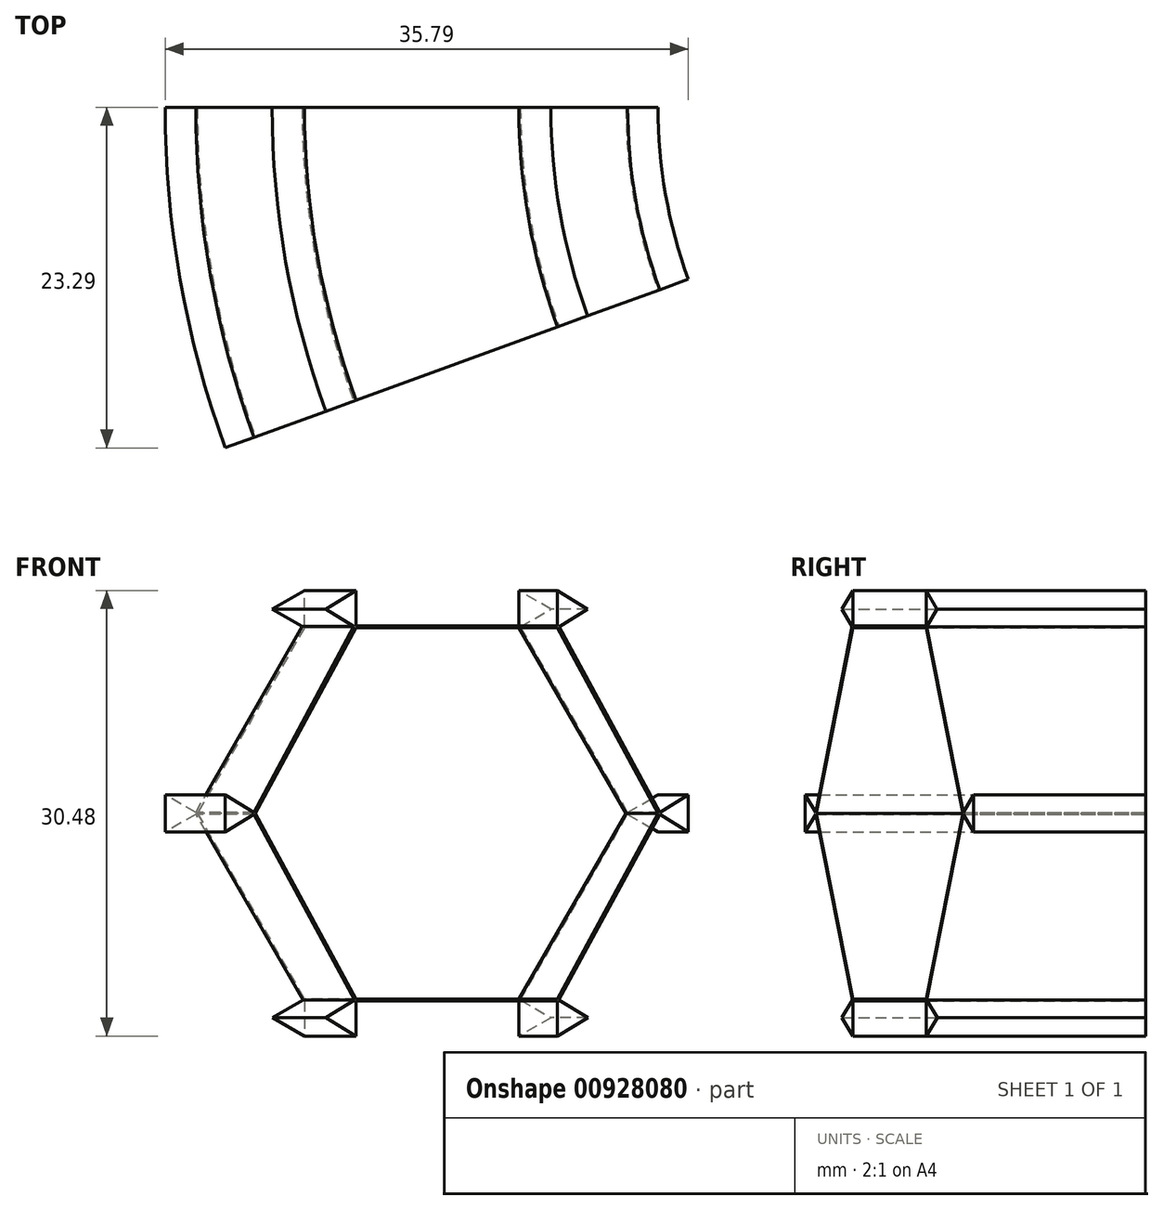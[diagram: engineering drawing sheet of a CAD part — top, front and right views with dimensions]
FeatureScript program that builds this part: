
annotation { "Feature Type Name" : "Feature", "Feature Type Description" : "" }
export const myFeature = defineFeature(function(context is Context, id is Id, definition is map)
    precondition{}
    {
        {
            var Q0;
            Q0=qCreatedBy(makeId("Top.planeOp"),FACE);
            var sketch = newSketch(context, id + "F0", { "sketchPlane" : qUnion([Q0])});
            skLineSegment(sketch, "E0", {"start": v(0, 0) * mm, "end": v(-50.8, 0) * mm});
            skCircle(sketch, "E1", {"center": v(0, 0) * mm, "radius": 50.8 * mm});
            skSolve(sketch);
        }
        {
            var Q0;
            Q0=qCreatedBy(makeId("Front.planeOp"),FACE);
            var sketch = newSketch(context, id + "F1", { "sketchPlane" : qUnion([Q0])});
            skPoint(sketch, "E2.0.midPoint", {"position": v(-51.22, 12.7) * mm});
            skLineSegment(sketch, "E3", {"start": v(-65.88, 0) * mm, "end": v(-68.08, -1.27) * mm});
            skLineSegment(sketch, "E4", {"start": v(-58.55, -12.7) * mm, "end": v(-60.75, -13.97) * mm});
            skLineSegment(sketch, "E5", {"start": v(-58.55, -12.7) * mm, "end": v(-58.55, -15.23) * mm});
            skLineSegment(sketch, "E6", {"start": v(-43.88, -12.7) * mm, "end": v(-43.88, -15.23) * mm});
            skLineSegment(sketch, "E7", {"start": v(-43.88, -12.7) * mm, "end": v(-41.67, -13.98) * mm});
            skLineSegment(sketch, "E8", {"start": v(-36.55, 0) * mm, "end": v(-34.36, -1.26) * mm});
            skLineSegment(sketch, "E9", {"start": v(-36.55, 0) * mm, "end": v(-34.36, 1.26) * mm});
            skLineSegment(sketch, "E10", {"start": v(-43.88, 12.7) * mm, "end": v(-41.7, 13.97) * mm});
            skLineSegment(sketch, "E11", {"start": v(-58.55, 12.7) * mm, "end": v(-58.55, 15.25) * mm});
            skLineSegment(sketch, "E12", {"start": v(-43.88, 12.7) * mm, "end": v(-43.88, 15.25) * mm});
            skLineSegment(sketch, "E13", {"start": v(-58.55, 12.7) * mm, "end": v(-60.76, 13.98) * mm});
            skLineSegment(sketch, "E14", {"start": v(-65.88, 0) * mm, "end": v(-68.08, 1.27) * mm});
            skLineSegment(sketch, "E15", {"start": v(-51.22, 12.7) * mm, "end": v(-51.22, 0) * mm});
            skLineSegment(sketch, "E16", {"start": v(-34.36, 1.26) * mm, "end": v(-34.36, -1.26) * mm});
            skLineSegment(sketch, "E17", {"start": v(-41.67, -13.98) * mm, "end": v(-43.88, -15.23) * mm});
            skLineSegment(sketch, "E18", {"start": v(-58.55, -15.23) * mm, "end": v(-60.75, -13.97) * mm});
            skLineSegment(sketch, "E19", {"start": v(-68.08, -1.27) * mm, "end": v(-68.08, 1.27) * mm});
            skLineSegment(sketch, "E20", {"start": v(-58.55, 15.25) * mm, "end": v(-60.76, 13.98) * mm});
            skLineSegment(sketch, "E21", {"start": v(-41.7, 13.97) * mm, "end": v(-43.88, 15.25) * mm});
            skLineSegment(sketch, "E22", {"start": v(-36.55, 0) * mm, "end": v(-36.33, -0.13) * mm});
            skLineSegment(sketch, "E23", {"start": v(-43.78, -12.76) * mm, "end": v(-43.88, -12.7) * mm});
            skLineSegment(sketch, "E24", {"start": v(-43.78, -12.76) * mm, "end": v(-36.44, -0.06) * mm});
            skLineSegment(sketch, "E25", {"start": v(-36.44, -0.06) * mm, "end": v(-36.55, 0) * mm});
            skLineSegment(sketch, "E26", {"start": v(-36.55, 0) * mm, "end": v(-43.88, -12.7) * mm});
            skLineSegment(sketch, "E27", {"start": v(-43.88, -12.7) * mm, "end": v(-43.88, -12.82) * mm});
            skLineSegment(sketch, "E28", {"start": v(-43.88, -12.82) * mm, "end": v(-58.55, -12.82) * mm});
            skLineSegment(sketch, "E29", {"start": v(-58.55, -12.82) * mm, "end": v(-58.55, -12.7) * mm});
            skLineSegment(sketch, "E30", {"start": v(-58.55, -12.7) * mm, "end": v(-43.88, -12.7) * mm});
            skLineSegment(sketch, "E31", {"start": v(-58.55, -12.7) * mm, "end": v(-58.66, -12.76) * mm});
            skLineSegment(sketch, "E32", {"start": v(-58.66, -12.76) * mm, "end": v(-65.95, -0.13) * mm});
            skLineSegment(sketch, "E33", {"start": v(-65.95, -0.13) * mm, "end": v(-66, -0.06) * mm});
            skLineSegment(sketch, "E34", {"start": v(-66, -0.06) * mm, "end": v(-65.88, 0) * mm});
            skLineSegment(sketch, "E35", {"start": v(-65.88, 0) * mm, "end": v(-58.55, -12.7) * mm});
            skLineSegment(sketch, "E36", {"start": v(-65.88, 0) * mm, "end": v(-66, 0.06) * mm});
            skLineSegment(sketch, "E37", {"start": v(-66, 0.06) * mm, "end": v(-58.71, 12.8) * mm});
            skLineSegment(sketch, "E38", {"start": v(-58.71, 12.8) * mm, "end": v(-58.55, 12.7) * mm});
            skLineSegment(sketch, "E39", {"start": v(-58.55, 12.7) * mm, "end": v(-65.88, 0) * mm});
            skLineSegment(sketch, "E40", {"start": v(-58.55, 12.7) * mm, "end": v(-58.55, 12.84) * mm});
            skLineSegment(sketch, "E41", {"start": v(-58.55, 12.84) * mm, "end": v(-43.88, 12.84) * mm});
            skLineSegment(sketch, "E42", {"start": v(-43.88, 12.84) * mm, "end": v(-43.88, 12.7) * mm});
            skLineSegment(sketch, "E43", {"start": v(-43.88, 12.7) * mm, "end": v(-58.55, 12.7) * mm});
            skLineSegment(sketch, "E44", {"start": v(-36.55, 0) * mm, "end": v(-36.44, 0.07) * mm});
            skLineSegment(sketch, "E45", {"start": v(-36.44, 0.07) * mm, "end": v(-43.78, 12.78) * mm});
            skLineSegment(sketch, "E46", {"start": v(-43.78, 12.78) * mm, "end": v(-43.88, 12.7) * mm});
            skLineSegment(sketch, "E47", {"start": v(-43.88, 12.7) * mm, "end": v(-36.55, 0) * mm});
            skSolve(sketch);
        }
        {
            var Q0;
            {var subQ3=sQuery(id+"F1.wireOp",EDGE,"E46");Q0=makeQuery(id+"F1.imprint","IMPRINT",FACE,{"disambiguationData":[TD([[makeQuery(id+"F1.imprint","IMPRINT",EDGE,{"derivedFrom":subQ3}),1.0]])]});}
            var Q1;
            {var subQ2=sQuery(id+"F1.wireOp",EDGE,"E16");Q1=makeQuery(id+"F1.imprint","IMPRINT",FACE,{"disambiguationData":[TD([[makeQuery(id+"F1.imprint","IMPRINT",EDGE,{"derivedFrom":subQ2}),-1.0]])]});}
            var Q2;
            {var subQ2=sQuery(id+"F1.wireOp",EDGE,"E20");Q2=makeQuery(id+"F1.imprint","IMPRINT",FACE,{"disambiguationData":[TD([[makeQuery(id+"F1.imprint","IMPRINT",EDGE,{"derivedFrom":subQ2}),1.0]])]});}
            var Q3;
            {var subQ4=sQuery(id+"F1.wireOp",EDGE,"E17");Q3=makeQuery(id+"F1.imprint","IMPRINT",FACE,{"disambiguationData":[TD([[makeQuery(id+"F1.imprint","IMPRINT",EDGE,{"derivedFrom":subQ4}),-1.0]])]});}
            var Q4;
            {var subQ4=sQuery(id+"F1.wireOp",EDGE,"E18");Q4=makeQuery(id+"F1.imprint","IMPRINT",FACE,{"disambiguationData":[TD([[makeQuery(id+"F1.imprint","IMPRINT",EDGE,{"derivedFrom":subQ4}),-1.0]])]});}
            var Q5;
            {var subQ4=sQuery(id+"F1.wireOp",EDGE,"E19");Q5=makeQuery(id+"F1.imprint","IMPRINT",FACE,{"disambiguationData":[TD([[makeQuery(id+"F1.imprint","IMPRINT",EDGE,{"derivedFrom":subQ4}),-1.0]])]});}
            var Q6;
            {var subQ3=sQuery(id+"F1.wireOp",EDGE,"E47");Q6=makeQuery(id+"F1.imprint","IMPRINT",FACE,{"disambiguationData":[TD([[makeQuery(id+"F1.imprint","IMPRINT",EDGE,{"derivedFrom":subQ3}),1.0]])]});}
            var Q7;
            {var subQ0=sQuery(id+"F1.wireOp",EDGE,"E24");Q7=makeQuery(id+"F1.imprint","IMPRINT",FACE,{"disambiguationData":[TD([[makeQuery(id+"F1.imprint","IMPRINT",EDGE,{"derivedFrom":subQ0}),1.0]])]});}
            var Q8;
            {var subQ4=sQuery(id+"F1.wireOp",EDGE,"E41");Q8=makeQuery(id+"F1.imprint","IMPRINT",FACE,{"disambiguationData":[TD([[makeQuery(id+"F1.imprint","IMPRINT",EDGE,{"derivedFrom":subQ4}),-1.0]])]});}
            var Q9;
            {var subQ2=sQuery(id+"F1.wireOp",EDGE,"E21");Q9=makeQuery(id+"F1.imprint","IMPRINT",FACE,{"disambiguationData":[TD([[makeQuery(id+"F1.imprint","IMPRINT",EDGE,{"derivedFrom":subQ2}),1.0]])]});}
            var Q10;
            {var subQ0=sQuery(id+"F1.wireOp",EDGE,"E37");Q10=makeQuery(id+"F1.imprint","IMPRINT",FACE,{"disambiguationData":[TD([[makeQuery(id+"F1.imprint","IMPRINT",EDGE,{"derivedFrom":subQ0}),-1.0]])]});}
            var Q11;
            {var subQ0=sQuery(id+"F1.wireOp",EDGE,"E28");Q11=makeQuery(id+"F1.imprint","IMPRINT",FACE,{"disambiguationData":[TD([[makeQuery(id+"F1.imprint","IMPRINT",EDGE,{"derivedFrom":subQ0}),-1.0]])]});}
            var Q12;
            {var subQ0=sQuery(id+"F1.wireOp",EDGE,"E32");Q12=makeQuery(id+"F1.imprint","IMPRINT",FACE,{"disambiguationData":[TD([[makeQuery(id+"F1.imprint","IMPRINT",EDGE,{"derivedFrom":subQ0}),-1.0]])]});}
            var Q13;
            Q13=sQuery(id+"F0.wireOp",EDGE,"E1");
            revolve(context, id + "F2", {"surfaceOperationType" : NewSurfaceOperationType.NEW, "entities" : qUnion([Q0, Q1, Q2, Q3, Q4, Q5, Q6, Q7, Q8, Q9, Q10, Q11, Q12]), "axis" : qUnion([Q13]), "revolveType" : RevolveType.ONE_DIRECTION, "angle" : 20 * degree});
        }
    });
